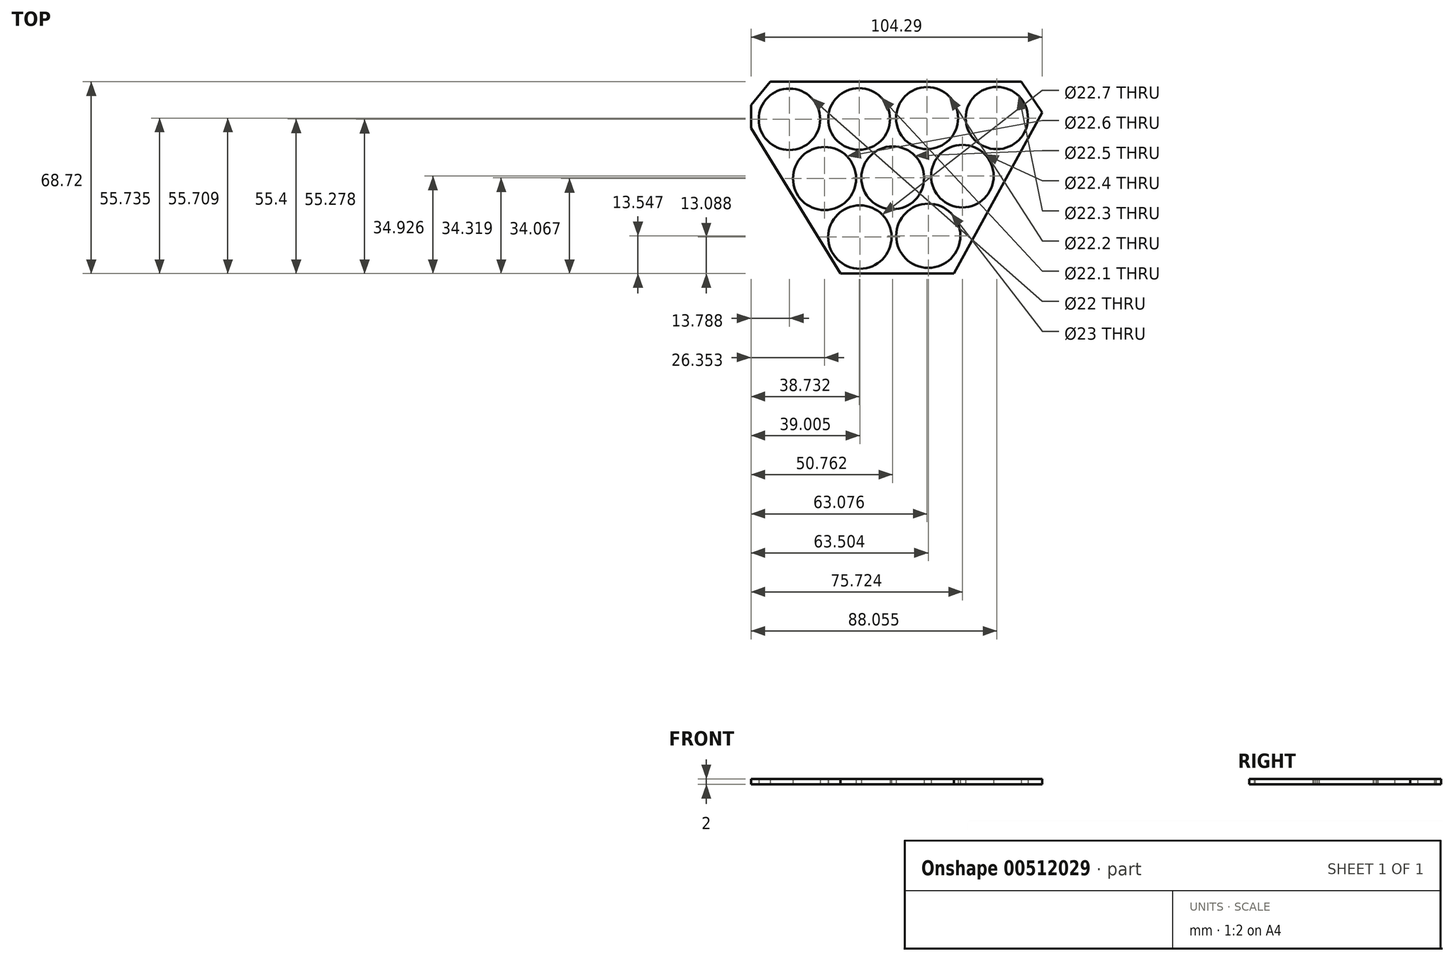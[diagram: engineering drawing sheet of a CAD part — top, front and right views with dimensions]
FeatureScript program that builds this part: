
annotation { "Feature Type Name" : "Feature", "Feature Type Description" : "" }
export const myFeature = defineFeature(function(context is Context, id is Id, definition is map)
    precondition{}
    {
        {
            var Q0;
            Q0=qCreatedBy(makeId("Top.planeOp"),FACE);
            var sketch = newSketch(context, id + "F0", { "sketchPlane" : qUnion([Q0])});
            skLineSegment(sketch, "E0.bottom", {"start": v(0, 0) * mm, "end": v(132.4, 0) * mm});
            skLineSegment(sketch, "E0.top", {"start": v(0, -114.56) * mm, "end": v(132.4, -114.56) * mm});
            skLineSegment(sketch, "E0.left", {"start": v(0, 0) * mm, "end": v(0, -114.56) * mm});
            skLineSegment(sketch, "E0.right", {"start": v(132.4, 0) * mm, "end": v(132.4, -114.56) * mm});
            skCircle(sketch, "E1", {"center": v(13.79, -13.44) * mm, "radius": 11 * mm});
            skCircle(sketch, "E2", {"center": v(38.73, -13.32) * mm, "radius": 11.05 * mm});
            skCircle(sketch, "E3", {"center": v(63.08, -13.01) * mm, "radius": 11.1 * mm});
            skCircle(sketch, "E4", {"center": v(88.06, -12.99) * mm, "radius": 11.15 * mm});
            skCircle(sketch, "E5", {"center": v(75.72, -33.8) * mm, "radius": 11.2 * mm});
            skCircle(sketch, "E6", {"center": v(50.76, -34.4) * mm, "radius": 11.25 * mm});
            skCircle(sketch, "E7", {"center": v(26.35, -34.65) * mm, "radius": 11.3 * mm});
            skCircle(sketch, "E8", {"center": v(39, -55.63) * mm, "radius": 11.35 * mm});
            skCircle(sketch, "E9", {"center": v(63.5, -55.17) * mm, "radius": 11.5 * mm});
            skLineSegment(sketch, "E10", {"start": v(0, -16.65) * mm, "end": v(32.03, -68.72) * mm});
            skLineSegment(sketch, "E11", {"start": v(32.03, -68.72) * mm, "end": v(72.68, -68.72) * mm});
            skLineSegment(sketch, "E12", {"start": v(72.68, -68.72) * mm, "end": v(110.32, 0) * mm});
            skLineSegment(sketch, "E13", {"start": v(0, -8.39) * mm, "end": v(6.92, 0) * mm});
            skLineSegment(sketch, "E14", {"start": v(96.8, 0) * mm, "end": v(104.29, -11.01) * mm});
            skSolve(sketch);
        }
        {
            var Q0;
            Q0=makeQuery(id+"F0.imprint","IMPRINT",FACE,{"disambiguationData":[TD([[makeQuery(id+"F0.imprint","IMPRINT",EDGE,{"derivedFrom":sQuery(id+"F0.wireOp",EDGE,"E1")}),-1.0]])]});
            extrude(context, id + "F1", {"entities" : qUnion([Q0]), "depth" : 2 * mm, "offsetDistance" : 25 * mm});
        }
    });
